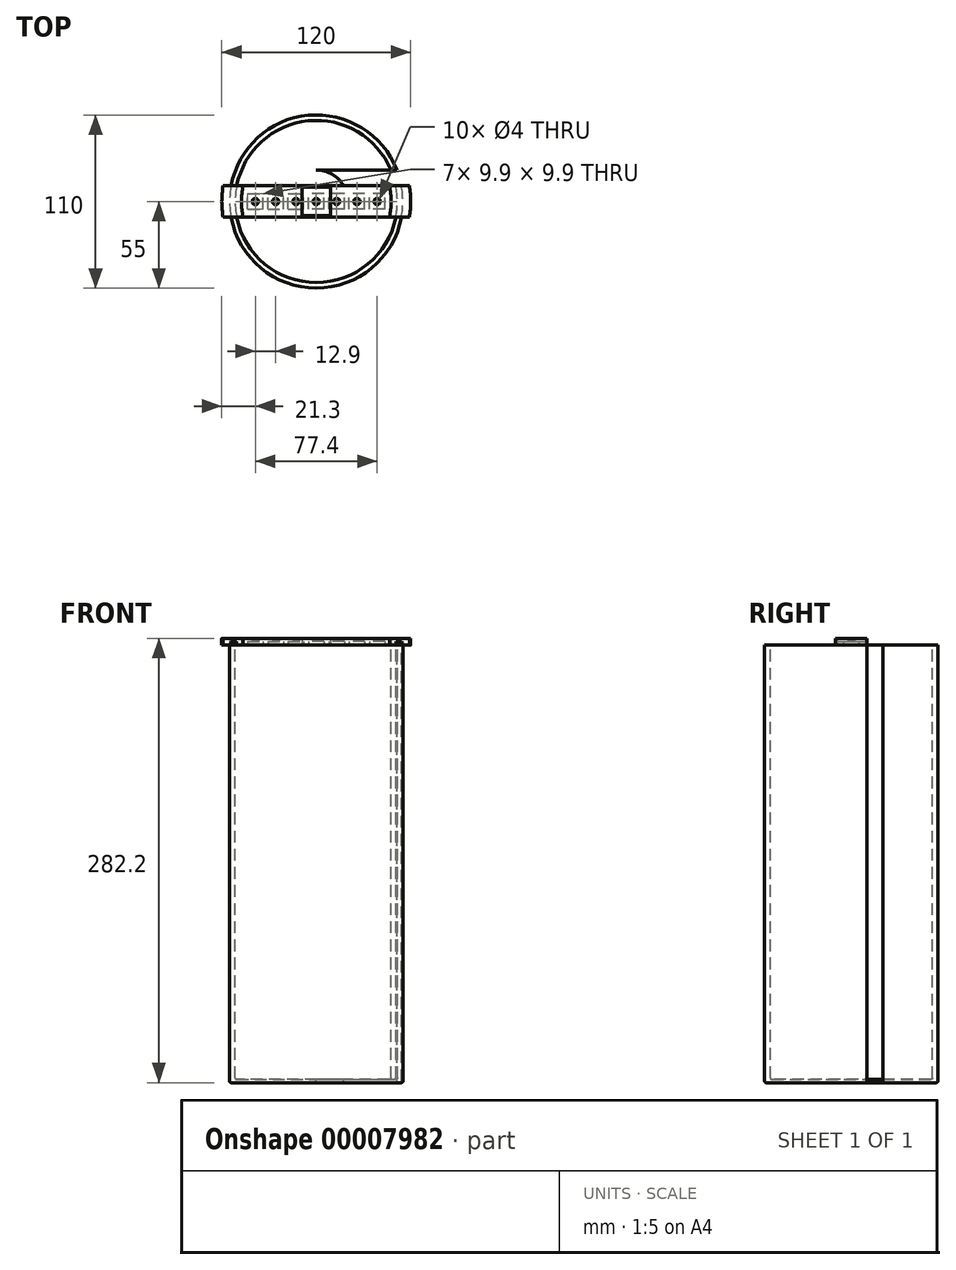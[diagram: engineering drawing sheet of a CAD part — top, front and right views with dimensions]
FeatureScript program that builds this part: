
annotation { "Feature Type Name" : "Feature", "Feature Type Description" : "" }
export const myFeature = defineFeature(function(context is Context, id is Id, definition is map)
    precondition{}
    {
        {
            var Q0;
            Q0=qCreatedBy(makeId("Top.planeOp"),FACE);
            var sketch = newSketch(context, id + "F0", { "sketchPlane" : qUnion([Q0])});
            skCircle(sketch, "E0", {"center": v(0, 0) * mm, "radius": 51.5 * mm});
            skCircle(sketch, "E1", {"center": v(0, 0) * mm, "radius": 4.8 * mm});
            skCircle(sketch, "E2", {"center": v(0, 12.6) * mm, "radius": 4.8 * mm});
            skLineSegment(sketch, "E3", {"start": v(0, 0) * mm, "end": v(0, 33.04) * mm, "construction": true});
            skCircle(sketch, "E4.1.0", {"center": v(-10.91, 6.3) * mm, "radius": 4.8 * mm});
            skCircle(sketch, "E4.2.0", {"center": v(-10.91, -6.3) * mm, "radius": 4.8 * mm});
            skCircle(sketch, "E4.3.0", {"center": v(0, -12.6) * mm, "radius": 4.8 * mm});
            skCircle(sketch, "E4.4.0", {"center": v(10.91, -6.3) * mm, "radius": 4.8 * mm});
            skCircle(sketch, "E4.5.0", {"center": v(10.91, 6.3) * mm, "radius": 4.8 * mm});
            skCircle(sketch, "E5", {"center": v(0, 0) * mm, "radius": 7.8 * mm, "construction": true});
            skCircle(sketch, "E6", {"center": v(0, 0) * mm, "radius": 20 * mm});
            skLineSegment(sketch, "E7.bottom", {"start": v(-65.9, 20) * mm, "end": v(65.9, 20) * mm});
            skLineSegment(sketch, "E7.top", {"start": v(-65.9, -20) * mm, "end": v(65.9, -20) * mm});
            skLineSegment(sketch, "E7.left", {"start": v(-65.9, 20) * mm, "end": v(-65.9, -20) * mm});
            skLineSegment(sketch, "E7.right", {"start": v(65.9, 20) * mm, "end": v(65.9, -20) * mm});
            skLineSegment(sketch, "E8", {"start": v(-65.9, 0) * mm, "end": v(65.9, 0) * mm, "construction": true});
            skCircle(sketch, "E9", {"center": v(0, 0) * mm, "radius": 55 * mm});
            skLineSegment(sketch, "E10", {"start": v(0, 20) * mm, "end": v(0, -20) * mm, "construction": true});
            skCircle(sketch, "E11", {"center": v(0, 0) * mm, "radius": 60 * mm});
            skCircle(sketch, "E12", {"center": v(0, 12.6) * mm, "radius": 1.75 * mm});
            skCircle(sketch, "E13", {"center": v(10.91, 6.3) * mm, "radius": 1.75 * mm});
            skCircle(sketch, "E14", {"center": v(10.91, -6.3) * mm, "radius": 1.75 * mm});
            skCircle(sketch, "E15", {"center": v(0, -12.6) * mm, "radius": 1.75 * mm});
            skCircle(sketch, "E16", {"center": v(-10.91, 6.3) * mm, "radius": 1.75 * mm});
            skCircle(sketch, "E17", {"center": v(-10.91, -6.3) * mm, "radius": 1.75 * mm});
            skCircle(sketch, "E18", {"center": v(0, 0) * mm, "radius": 1.75 * mm});
            skLineSegment(sketch, "E19.bottom", {"start": v(-65.9, -10) * mm, "end": v(-17.32, -10) * mm});
            skLineSegment(sketch, "E19.top", {"start": v(-65.9, 10) * mm, "end": v(-17.32, 10) * mm});
            skLineSegment(sketch, "E19.left", {"start": v(-65.9, -10) * mm, "end": v(-65.9, 10) * mm});
            skLineSegment(sketch, "E19.right", {"start": v(65.9, -10) * mm, "end": v(65.9, 10) * mm});
            skLineSegment(sketch, "E20.trimOffspring", {"start": v(17.32, -10) * mm, "end": v(65.9, -10) * mm});
            skLineSegment(sketch, "E21.trimOffspring", {"start": v(17.32, 10) * mm, "end": v(65.9, 10) * mm});
            skLineSegment(sketch, "E22.bottom", {"start": v(-24, -5) * mm, "end": v(-47.5, -5) * mm});
            skLineSegment(sketch, "E22.top", {"start": v(-24, 5) * mm, "end": v(-47.5, 5) * mm});
            skLineSegment(sketch, "E22.left", {"start": v(-24, -5) * mm, "end": v(-24, 5) * mm});
            skLineSegment(sketch, "E22.right", {"start": v(-47.5, -5) * mm, "end": v(-47.5, 5) * mm});
            skPoint(sketch, "E22.middle", {"position": v(-35.75, 0) * mm});
            skLineSegment(sketch, "E23.MirrorCS", {"start": v(24, 5) * mm, "end": v(47.5, 5) * mm});
            skLineSegment(sketch, "E24.MirrorCS", {"start": v(24, -5) * mm, "end": v(24, 5) * mm});
            skLineSegment(sketch, "E25.MirrorCS", {"start": v(24, -5) * mm, "end": v(47.5, -5) * mm});
            skLineSegment(sketch, "E26.MirrorCS", {"start": v(47.5, -5) * mm, "end": v(47.5, 5) * mm});
            skSolve(sketch);
        }
        {
            var Q0;
            {var subQ0=sQuery(id+"F0.wireOp",EDGE,"E7.bottom");var subQ1=sQuery(id+"F0.wireOp",EDGE,"E0");var subQ2=makeQuery(id+"F0.imprint","INTERSECT",VERTEX,{"disambiguationData":[OD(0.0)],"derivedFrom":[subQ1,subQ0]});Q0=makeQuery(id+"F0.imprint","IMPRINT",FACE,{"disambiguationData":[TD([[makeQuery(id+"F0.imprint","IMPRINT",EDGE,{"disambiguationData":[TD([[subQ2,-1.0]])],"derivedFrom":subQ1}),-1.0]])]});}
            var Q1;
            {var subQ0=sQuery(id+"F0.wireOp",EDGE,"E7.bottom");var subQ1=sQuery(id+"F0.wireOp",EDGE,"E0");var subQ2=makeQuery(id+"F0.imprint","INTERSECT",VERTEX,{"disambiguationData":[OD(1.0)],"derivedFrom":[subQ1,subQ0]});Q1=makeQuery(id+"F0.imprint","IMPRINT",FACE,{"disambiguationData":[TD([[makeQuery(id+"F0.imprint","IMPRINT",EDGE,{"disambiguationData":[TD([[subQ2,-1.0]])],"derivedFrom":subQ1}),-1.0]])]});}
            var Q2;
            {var subQ0=sQuery(id+"F0.wireOp",EDGE,"E19.top");var subQ1=sQuery(id+"F0.wireOp",EDGE,"E0");var subQ2=makeQuery(id+"F0.imprint","INTERSECT",VERTEX,{"derivedFrom":[subQ1,subQ0]});Q2=makeQuery(id+"F0.imprint","IMPRINT",FACE,{"disambiguationData":[TD([[makeQuery(id+"F0.imprint","IMPRINT",EDGE,{"disambiguationData":[TD([[subQ2,-1.0]])],"derivedFrom":subQ1}),-1.0]])]});}
            var Q3;
            {var subQ0=sQuery(id+"F0.wireOp",EDGE,"E19.bottom");var subQ1=sQuery(id+"F0.wireOp",EDGE,"E0");var subQ2=makeQuery(id+"F0.imprint","INTERSECT",VERTEX,{"derivedFrom":[subQ1,subQ0]});Q3=makeQuery(id+"F0.imprint","IMPRINT",FACE,{"disambiguationData":[TD([[makeQuery(id+"F0.imprint","IMPRINT",EDGE,{"disambiguationData":[TD([[subQ2,-1.0]])],"derivedFrom":subQ1}),-1.0]])]});}
            var Q4;
            {var subQ0=sQuery(id+"F0.wireOp",EDGE,"E7.top");var subQ1=sQuery(id+"F0.wireOp",EDGE,"E0");var subQ2=makeQuery(id+"F0.imprint","INTERSECT",VERTEX,{"disambiguationData":[OD(0.0)],"derivedFrom":[subQ1,subQ0]});Q4=makeQuery(id+"F0.imprint","IMPRINT",FACE,{"disambiguationData":[TD([[makeQuery(id+"F0.imprint","IMPRINT",EDGE,{"disambiguationData":[TD([[subQ2,-1.0]])],"derivedFrom":subQ1}),-1.0]])]});}
            var Q5;
            {var subQ0=sQuery(id+"F0.wireOp",EDGE,"E7.top");var subQ1=sQuery(id+"F0.wireOp",EDGE,"E0");var subQ2=makeQuery(id+"F0.imprint","INTERSECT",VERTEX,{"disambiguationData":[OD(1.0)],"derivedFrom":[subQ1,subQ0]});Q5=makeQuery(id+"F0.imprint","IMPRINT",FACE,{"disambiguationData":[TD([[makeQuery(id+"F0.imprint","IMPRINT",EDGE,{"disambiguationData":[TD([[subQ2,-1.0]])],"derivedFrom":subQ1}),-1.0]])]});}
            var Q6;
            {var subQ0=sQuery(id+"F0.wireOp",EDGE,"E21.trimOffspring");var subQ1=sQuery(id+"F0.wireOp",EDGE,"E0");var subQ2=makeQuery(id+"F0.imprint","INTERSECT",VERTEX,{"derivedFrom":[subQ1,subQ0]});Q6=makeQuery(id+"F0.imprint","IMPRINT",FACE,{"disambiguationData":[TD([[makeQuery(id+"F0.imprint","IMPRINT",EDGE,{"disambiguationData":[TD([[subQ2,1.0]])],"derivedFrom":subQ1}),-1.0]])]});}
            var Q7;
            {var subQ0=sQuery(id+"F0.wireOp",EDGE,"E7.bottom");var subQ1=sQuery(id+"F0.wireOp",EDGE,"E0");var subQ2=makeQuery(id+"F0.imprint","INTERSECT",VERTEX,{"disambiguationData":[OD(0.0)],"derivedFrom":[subQ1,subQ0]});Q7=makeQuery(id+"F0.imprint","IMPRINT",FACE,{"disambiguationData":[TD([[makeQuery(id+"F0.imprint","IMPRINT",EDGE,{"disambiguationData":[TD([[subQ2,1.0]])],"derivedFrom":subQ1}),-1.0]])]});}
            var Q8;
            {var subQ0=sQuery(id+"F0.wireOp",EDGE,"E19.top");var subQ1=sQuery(id+"F0.wireOp",EDGE,"E0");var subQ2=makeQuery(id+"F0.imprint","INTERSECT",VERTEX,{"derivedFrom":[subQ1,subQ0]});Q8=makeQuery(id+"F0.imprint","IMPRINT",FACE,{"disambiguationData":[TD([[makeQuery(id+"F0.imprint","IMPRINT",EDGE,{"disambiguationData":[TD([[subQ2,-1.0]])],"derivedFrom":subQ1}),1.0]])]});}
            var Q9;
            Q9=makeQuery(id+"F0.imprint","IMPRINT",FACE,{"disambiguationData":[TD([[makeQuery(id+"F0.imprint","IMPRINT",EDGE,{"derivedFrom":sQuery(id+"F0.wireOp",EDGE,"E4.2.0")}),1.0]])]});
            var Q10;
            {var subQ0=sQuery(id+"F0.wireOp",EDGE,"E7.bottom");var subQ1=sQuery(id+"F0.wireOp",EDGE,"E0");var subQ2=makeQuery(id+"F0.imprint","INTERSECT",VERTEX,{"disambiguationData":[OD(1.0)],"derivedFrom":[subQ1,subQ0]});Q10=makeQuery(id+"F0.imprint","IMPRINT",FACE,{"disambiguationData":[TD([[makeQuery(id+"F0.imprint","IMPRINT",EDGE,{"disambiguationData":[TD([[subQ2,-1.0]])],"derivedFrom":subQ1}),1.0]])]});}
            var Q11;
            {var subQ0=sQuery(id+"F0.wireOp",EDGE,"E7.bottom");var subQ1=sQuery(id+"F0.wireOp",EDGE,"E0");var subQ2=makeQuery(id+"F0.imprint","INTERSECT",VERTEX,{"disambiguationData":[OD(0.0)],"derivedFrom":[subQ1,subQ0]});Q11=makeQuery(id+"F0.imprint","IMPRINT",FACE,{"disambiguationData":[TD([[makeQuery(id+"F0.imprint","IMPRINT",EDGE,{"disambiguationData":[TD([[subQ2,-1.0]])],"derivedFrom":subQ1}),1.0]])]});}
            var Q12;
            {var subQ0=sQuery(id+"F0.wireOp",EDGE,"E19.bottom");var subQ1=sQuery(id+"F0.wireOp",EDGE,"E0");var subQ2=makeQuery(id+"F0.imprint","INTERSECT",VERTEX,{"derivedFrom":[subQ1,subQ0]});Q12=makeQuery(id+"F0.imprint","IMPRINT",FACE,{"disambiguationData":[TD([[makeQuery(id+"F0.imprint","IMPRINT",EDGE,{"disambiguationData":[TD([[subQ2,-1.0]])],"derivedFrom":subQ1}),1.0]])]});}
            var Q13;
            Q13=makeQuery(id+"F0.imprint","IMPRINT",FACE,{"disambiguationData":[TD([[makeQuery(id+"F0.imprint","IMPRINT",EDGE,{"derivedFrom":sQuery(id+"F0.wireOp",EDGE,"E17")}),1.0]])]});
            var Q14;
            {var subQ0=sQuery(id+"F0.wireOp",EDGE,"E7.top");var subQ1=sQuery(id+"F0.wireOp",EDGE,"E0");var subQ2=makeQuery(id+"F0.imprint","INTERSECT",VERTEX,{"disambiguationData":[OD(0.0)],"derivedFrom":[subQ1,subQ0]});Q14=makeQuery(id+"F0.imprint","IMPRINT",FACE,{"disambiguationData":[TD([[makeQuery(id+"F0.imprint","IMPRINT",EDGE,{"disambiguationData":[TD([[subQ2,-1.0]])],"derivedFrom":subQ1}),1.0]])]});}
            var Q15;
            {var subQ0=sQuery(id+"F0.wireOp",EDGE,"E7.bottom");var subQ1=sQuery(id+"F0.wireOp",EDGE,"E0");var subQ2=makeQuery(id+"F0.imprint","INTERSECT",VERTEX,{"disambiguationData":[OD(0.0)],"derivedFrom":[subQ1,subQ0]});Q15=makeQuery(id+"F0.imprint","IMPRINT",FACE,{"disambiguationData":[TD([[makeQuery(id+"F0.imprint","IMPRINT",EDGE,{"disambiguationData":[TD([[subQ2,1.0]])],"derivedFrom":subQ1}),1.0]])]});}
            var Q16;
            {var subQ0=sQuery(id+"F0.wireOp",EDGE,"E21.trimOffspring");var subQ1=sQuery(id+"F0.wireOp",EDGE,"E0");var subQ2=makeQuery(id+"F0.imprint","INTERSECT",VERTEX,{"derivedFrom":[subQ1,subQ0]});Q16=makeQuery(id+"F0.imprint","IMPRINT",FACE,{"disambiguationData":[TD([[makeQuery(id+"F0.imprint","IMPRINT",EDGE,{"disambiguationData":[TD([[subQ2,1.0]])],"derivedFrom":subQ1}),1.0]])]});}
            var Q17;
            {var subQ0=sQuery(id+"F0.wireOp",EDGE,"E7.top");var subQ1=sQuery(id+"F0.wireOp",EDGE,"E0");var subQ2=makeQuery(id+"F0.imprint","INTERSECT",VERTEX,{"disambiguationData":[OD(1.0)],"derivedFrom":[subQ1,subQ0]});Q17=makeQuery(id+"F0.imprint","IMPRINT",FACE,{"disambiguationData":[TD([[makeQuery(id+"F0.imprint","IMPRINT",EDGE,{"disambiguationData":[TD([[subQ2,-1.0]])],"derivedFrom":subQ1}),1.0]])]});}
            var Q18;
            Q18=makeQuery(id+"F0.imprint","IMPRINT",FACE,{"disambiguationData":[TD([[makeQuery(id+"F0.imprint","IMPRINT",EDGE,{"derivedFrom":sQuery(id+"F0.wireOp",EDGE,"E1")}),-1.0]])]});
            var Q19;
            Q19=makeQuery(id+"F0.imprint","IMPRINT",FACE,{"disambiguationData":[TD([[makeQuery(id+"F0.imprint","IMPRINT",EDGE,{"derivedFrom":sQuery(id+"F0.wireOp",EDGE,"E4.1.0")}),1.0]])]});
            var Q20;
            Q20=makeQuery(id+"F0.imprint","IMPRINT",FACE,{"disambiguationData":[TD([[makeQuery(id+"F0.imprint","IMPRINT",EDGE,{"derivedFrom":sQuery(id+"F0.wireOp",EDGE,"E2")}),1.0]])]});
            var Q21;
            Q21=makeQuery(id+"F0.imprint","IMPRINT",FACE,{"disambiguationData":[TD([[makeQuery(id+"F0.imprint","IMPRINT",EDGE,{"derivedFrom":sQuery(id+"F0.wireOp",EDGE,"E1")}),1.0]])]});
            var Q22;
            Q22=makeQuery(id+"F0.imprint","IMPRINT",FACE,{"disambiguationData":[TD([[makeQuery(id+"F0.imprint","IMPRINT",EDGE,{"derivedFrom":sQuery(id+"F0.wireOp",EDGE,"E4.5.0")}),1.0]])]});
            var Q23;
            Q23=makeQuery(id+"F0.imprint","IMPRINT",FACE,{"disambiguationData":[TD([[makeQuery(id+"F0.imprint","IMPRINT",EDGE,{"derivedFrom":sQuery(id+"F0.wireOp",EDGE,"E4.4.0")}),1.0]])]});
            var Q24;
            Q24=makeQuery(id+"F0.imprint","IMPRINT",FACE,{"disambiguationData":[TD([[makeQuery(id+"F0.imprint","IMPRINT",EDGE,{"derivedFrom":sQuery(id+"F0.wireOp",EDGE,"E4.3.0")}),1.0]])]});
            var Q25;
            Q25=makeQuery(id+"F0.imprint","IMPRINT",FACE,{"disambiguationData":[TD([[makeQuery(id+"F0.imprint","IMPRINT",EDGE,{"derivedFrom":sQuery(id+"F0.wireOp",EDGE,"E16")}),1.0]])]});
            var Q26;
            Q26=makeQuery(id+"F0.imprint","IMPRINT",FACE,{"disambiguationData":[TD([[makeQuery(id+"F0.imprint","IMPRINT",EDGE,{"derivedFrom":sQuery(id+"F0.wireOp",EDGE,"E12")}),1.0]])]});
            var Q27;
            Q27=makeQuery(id+"F0.imprint","IMPRINT",FACE,{"disambiguationData":[TD([[makeQuery(id+"F0.imprint","IMPRINT",EDGE,{"derivedFrom":sQuery(id+"F0.wireOp",EDGE,"E13")}),1.0]])]});
            var Q28;
            Q28=makeQuery(id+"F0.imprint","IMPRINT",FACE,{"disambiguationData":[TD([[makeQuery(id+"F0.imprint","IMPRINT",EDGE,{"derivedFrom":sQuery(id+"F0.wireOp",EDGE,"E14")}),1.0]])]});
            var Q29;
            Q29=makeQuery(id+"F0.imprint","IMPRINT",FACE,{"disambiguationData":[TD([[makeQuery(id+"F0.imprint","IMPRINT",EDGE,{"derivedFrom":sQuery(id+"F0.wireOp",EDGE,"E18")}),1.0]])]});
            var Q30;
            Q30=makeQuery(id+"F0.imprint","IMPRINT",FACE,{"disambiguationData":[TD([[makeQuery(id+"F0.imprint","IMPRINT",EDGE,{"derivedFrom":sQuery(id+"F0.wireOp",EDGE,"E15")}),1.0]])]});
            var Q31;
            Q31=makeQuery(id+"F0.imprint","IMPRINT",FACE,{"disambiguationData":[TD([[makeQuery(id+"F0.imprint","IMPRINT",EDGE,{"derivedFrom":sQuery(id+"F0.wireOp",EDGE,"E22.bottom")}),-1.0]])]});
            var Q32;
            Q32=makeQuery(id+"F0.imprint","IMPRINT",FACE,{"disambiguationData":[TD([[makeQuery(id+"F0.imprint","IMPRINT",EDGE,{"derivedFrom":sQuery(id+"F0.wireOp",EDGE,"E23.MirrorCS")}),-1.0]])]});
            extrude(context, id + "F1", {"entities" : qUnion([Q0, Q1, Q2, Q3, Q4, Q5, Q6, Q7, Q8, Q9, Q10, Q11, Q12, Q13, Q14, Q15, Q16, Q17, Q18, Q19, Q20, Q21, Q22, Q23, Q24, Q25, Q26, Q27, Q28, Q29, Q30, Q31, Q32]), "oppositeDirection" : true, "depth" : 278 * mm});
        }
        {
            var Q0;
            {var subQ0=sQuery(id+"F0.wireOp",EDGE,"E7.bottom");var subQ1=sQuery(id+"F0.wireOp",EDGE,"E0");var subQ2=makeQuery(id+"F0.imprint","INTERSECT",VERTEX,{"disambiguationData":[OD(0.0)],"derivedFrom":[subQ1,subQ0]});Q0=makeQuery(id+"F0.imprint","IMPRINT",FACE,{"disambiguationData":[TD([[makeQuery(id+"F0.imprint","IMPRINT",EDGE,{"disambiguationData":[TD([[subQ2,-1.0]])],"derivedFrom":subQ1}),1.0]])]});}
            var Q1;
            {var subQ0=sQuery(id+"F0.wireOp",EDGE,"E7.bottom");var subQ1=sQuery(id+"F0.wireOp",EDGE,"E0");var subQ2=makeQuery(id+"F0.imprint","INTERSECT",VERTEX,{"disambiguationData":[OD(0.0)],"derivedFrom":[subQ1,subQ0]});Q1=makeQuery(id+"F0.imprint","IMPRINT",FACE,{"disambiguationData":[TD([[makeQuery(id+"F0.imprint","IMPRINT",EDGE,{"disambiguationData":[TD([[subQ2,1.0]])],"derivedFrom":subQ1}),1.0]])]});}
            var Q2;
            {var subQ0=sQuery(id+"F0.wireOp",EDGE,"E21.trimOffspring");var subQ1=sQuery(id+"F0.wireOp",EDGE,"E0");var subQ2=makeQuery(id+"F0.imprint","INTERSECT",VERTEX,{"derivedFrom":[subQ1,subQ0]});Q2=makeQuery(id+"F0.imprint","IMPRINT",FACE,{"disambiguationData":[TD([[makeQuery(id+"F0.imprint","IMPRINT",EDGE,{"disambiguationData":[TD([[subQ2,1.0]])],"derivedFrom":subQ1}),1.0]])]});}
            var Q3;
            {var subQ0=sQuery(id+"F0.wireOp",EDGE,"E7.top");var subQ1=sQuery(id+"F0.wireOp",EDGE,"E0");var subQ2=makeQuery(id+"F0.imprint","INTERSECT",VERTEX,{"disambiguationData":[OD(1.0)],"derivedFrom":[subQ1,subQ0]});Q3=makeQuery(id+"F0.imprint","IMPRINT",FACE,{"disambiguationData":[TD([[makeQuery(id+"F0.imprint","IMPRINT",EDGE,{"disambiguationData":[TD([[subQ2,-1.0]])],"derivedFrom":subQ1}),1.0]])]});}
            var Q4;
            {var subQ0=sQuery(id+"F0.wireOp",EDGE,"E7.top");var subQ1=sQuery(id+"F0.wireOp",EDGE,"E0");var subQ2=makeQuery(id+"F0.imprint","INTERSECT",VERTEX,{"disambiguationData":[OD(0.0)],"derivedFrom":[subQ1,subQ0]});Q4=makeQuery(id+"F0.imprint","IMPRINT",FACE,{"disambiguationData":[TD([[makeQuery(id+"F0.imprint","IMPRINT",EDGE,{"disambiguationData":[TD([[subQ2,-1.0]])],"derivedFrom":subQ1}),1.0]])]});}
            var Q5;
            {var subQ0=sQuery(id+"F0.wireOp",EDGE,"E19.bottom");var subQ1=sQuery(id+"F0.wireOp",EDGE,"E0");var subQ2=makeQuery(id+"F0.imprint","INTERSECT",VERTEX,{"derivedFrom":[subQ1,subQ0]});Q5=makeQuery(id+"F0.imprint","IMPRINT",FACE,{"disambiguationData":[TD([[makeQuery(id+"F0.imprint","IMPRINT",EDGE,{"disambiguationData":[TD([[subQ2,-1.0]])],"derivedFrom":subQ1}),1.0]])]});}
            var Q6;
            {var subQ0=sQuery(id+"F0.wireOp",EDGE,"E7.bottom");var subQ1=sQuery(id+"F0.wireOp",EDGE,"E0");var subQ2=makeQuery(id+"F0.imprint","INTERSECT",VERTEX,{"disambiguationData":[OD(1.0)],"derivedFrom":[subQ1,subQ0]});Q6=makeQuery(id+"F0.imprint","IMPRINT",FACE,{"disambiguationData":[TD([[makeQuery(id+"F0.imprint","IMPRINT",EDGE,{"disambiguationData":[TD([[subQ2,-1.0]])],"derivedFrom":subQ1}),1.0]])]});}
            var Q7;
            {var subQ0=sQuery(id+"F0.wireOp",EDGE,"E19.top");var subQ1=sQuery(id+"F0.wireOp",EDGE,"E0");var subQ2=makeQuery(id+"F0.imprint","INTERSECT",VERTEX,{"derivedFrom":[subQ1,subQ0]});Q7=makeQuery(id+"F0.imprint","IMPRINT",FACE,{"disambiguationData":[TD([[makeQuery(id+"F0.imprint","IMPRINT",EDGE,{"disambiguationData":[TD([[subQ2,-1.0]])],"derivedFrom":subQ1}),1.0]])]});}
            var Q8;
            Q8=makeQuery(id+"F0.imprint","IMPRINT",FACE,{"disambiguationData":[TD([[makeQuery(id+"F0.imprint","IMPRINT",EDGE,{"derivedFrom":sQuery(id+"F0.wireOp",EDGE,"E1")}),-1.0]])]});
            var Q9;
            Q9=makeQuery(id+"F0.imprint","IMPRINT",FACE,{"disambiguationData":[TD([[makeQuery(id+"F0.imprint","IMPRINT",EDGE,{"derivedFrom":sQuery(id+"F0.wireOp",EDGE,"E4.4.0")}),1.0]])]});
            var Q10;
            Q10=makeQuery(id+"F0.imprint","IMPRINT",FACE,{"disambiguationData":[TD([[makeQuery(id+"F0.imprint","IMPRINT",EDGE,{"derivedFrom":sQuery(id+"F0.wireOp",EDGE,"E14")}),1.0]])]});
            var Q11;
            Q11=makeQuery(id+"F0.imprint","IMPRINT",FACE,{"disambiguationData":[TD([[makeQuery(id+"F0.imprint","IMPRINT",EDGE,{"derivedFrom":sQuery(id+"F0.wireOp",EDGE,"E13")}),1.0]])]});
            var Q12;
            Q12=makeQuery(id+"F0.imprint","IMPRINT",FACE,{"disambiguationData":[TD([[makeQuery(id+"F0.imprint","IMPRINT",EDGE,{"derivedFrom":sQuery(id+"F0.wireOp",EDGE,"E4.5.0")}),1.0]])]});
            var Q13;
            Q13=makeQuery(id+"F0.imprint","IMPRINT",FACE,{"disambiguationData":[TD([[makeQuery(id+"F0.imprint","IMPRINT",EDGE,{"derivedFrom":sQuery(id+"F0.wireOp",EDGE,"E2")}),1.0]])]});
            var Q14;
            Q14=makeQuery(id+"F0.imprint","IMPRINT",FACE,{"disambiguationData":[TD([[makeQuery(id+"F0.imprint","IMPRINT",EDGE,{"derivedFrom":sQuery(id+"F0.wireOp",EDGE,"E12")}),1.0]])]});
            var Q15;
            Q15=makeQuery(id+"F0.imprint","IMPRINT",FACE,{"disambiguationData":[TD([[makeQuery(id+"F0.imprint","IMPRINT",EDGE,{"derivedFrom":sQuery(id+"F0.wireOp",EDGE,"E4.1.0")}),1.0]])]});
            var Q16;
            Q16=makeQuery(id+"F0.imprint","IMPRINT",FACE,{"disambiguationData":[TD([[makeQuery(id+"F0.imprint","IMPRINT",EDGE,{"derivedFrom":sQuery(id+"F0.wireOp",EDGE,"E16")}),1.0]])]});
            var Q17;
            Q17=makeQuery(id+"F0.imprint","IMPRINT",FACE,{"disambiguationData":[TD([[makeQuery(id+"F0.imprint","IMPRINT",EDGE,{"derivedFrom":sQuery(id+"F0.wireOp",EDGE,"E4.2.0")}),1.0]])]});
            var Q18;
            Q18=makeQuery(id+"F0.imprint","IMPRINT",FACE,{"disambiguationData":[TD([[makeQuery(id+"F0.imprint","IMPRINT",EDGE,{"derivedFrom":sQuery(id+"F0.wireOp",EDGE,"E17")}),1.0]])]});
            var Q19;
            Q19=makeQuery(id+"F0.imprint","IMPRINT",FACE,{"disambiguationData":[TD([[makeQuery(id+"F0.imprint","IMPRINT",EDGE,{"derivedFrom":sQuery(id+"F0.wireOp",EDGE,"E4.3.0")}),1.0]])]});
            var Q20;
            Q20=makeQuery(id+"F0.imprint","IMPRINT",FACE,{"disambiguationData":[TD([[makeQuery(id+"F0.imprint","IMPRINT",EDGE,{"derivedFrom":sQuery(id+"F0.wireOp",EDGE,"E15")}),1.0]])]});
            var Q21;
            Q21=makeQuery(id+"F0.imprint","IMPRINT",FACE,{"disambiguationData":[TD([[makeQuery(id+"F0.imprint","IMPRINT",EDGE,{"derivedFrom":sQuery(id+"F0.wireOp",EDGE,"E1")}),1.0]])]});
            var Q22;
            Q22=makeQuery(id+"F0.imprint","IMPRINT",FACE,{"disambiguationData":[TD([[makeQuery(id+"F0.imprint","IMPRINT",EDGE,{"derivedFrom":sQuery(id+"F0.wireOp",EDGE,"E18")}),1.0]])]});
            var Q23;
            Q23=makeQuery(id+"F0.imprint","IMPRINT",FACE,{"disambiguationData":[TD([[makeQuery(id+"F0.imprint","IMPRINT",EDGE,{"derivedFrom":sQuery(id+"F0.wireOp",EDGE,"E22.bottom")}),-1.0]])]});
            var Q24;
            Q24=makeQuery(id+"F0.imprint","IMPRINT",FACE,{"disambiguationData":[TD([[makeQuery(id+"F0.imprint","IMPRINT",EDGE,{"derivedFrom":sQuery(id+"F0.wireOp",EDGE,"E23.MirrorCS")}),-1.0]])]});
            extrude(context, id + "F2", {"entities" : qUnion([Q0, Q1, Q2, Q3, Q4, Q5, Q6, Q7, Q8, Q9, Q10, Q11, Q12, Q13, Q14, Q15, Q16, Q17, Q18, Q19, Q20, Q21, Q22, Q23, Q24]), "operationType" : NewBodyOperationType.REMOVE, "oppositeDirection" : true, "depth" : 276 * mm});
        }
        {
            var Q0;
            Q0=makeQuery(id+"F2.boolean.opBoolean","COPY",EDGE,{"derivedFrom":makeQuery(id+"F2.opExtrude","CAP_EDGE",EDGE,{"disambiguationData":[OSD([sQuery(id+"F0.wireOp",EDGE,"E0")])],"isStart":false})});
            var Q1;
            Q1=makeQuery(id+"F1.opExtrude","CAP_EDGE",EDGE,{"disambiguationData":[OSD([sQuery(id+"F0.wireOp",EDGE,"E9")])],"isStart":false});
            fillet(context, id + "F3", {"entities" : qUnion([Q0, Q1]), "radius" : 1 * mm, "tangentPropagation" : true, "allowEdgeOverflow" : false});
        }
        {
            var Q0;
            Q0=qCreatedBy(makeId("Top.planeOp"),FACE);
            var sketch = newSketch(context, id + "F4", { "sketchPlane" : qUnion([Q0])});
            skLineSegment(sketch, "E27.0", {"start": v(-59.16, 10) * mm, "end": v(-17.32, 10) * mm});
            skLineSegment(sketch, "E27.1", {"start": v(17.32, 10) * mm, "end": v(59.16, 10) * mm});
            skLineSegment(sketch, "E27.2", {"start": v(17.32, -10) * mm, "end": v(59.16, -10) * mm});
            skLineSegment(sketch, "E27.3", {"start": v(-59.16, -10) * mm, "end": v(-17.32, -10) * mm});
            skCircle(sketch, "E27.4", {"center": v(0, 0) * mm, "radius": 60 * mm});
            skCircle(sketch, "E27.5", {"center": v(0, 0) * mm, "radius": 51.5 * mm});
            skCircle(sketch, "E27.6", {"center": v(0, 0) * mm, "radius": 55 * mm});
            skLineSegment(sketch, "E28.0", {"start": v(0, 0) * mm, "end": v(0, 33.04) * mm, "construction": true});
            skLineSegment(sketch, "E28.1", {"start": v(0, 20) * mm, "end": v(0, -20) * mm, "construction": true});
            skLineSegment(sketch, "E29", {"start": v(-17.32, 10) * mm, "end": v(17.32, 10) * mm});
            skLineSegment(sketch, "E30", {"start": v(-17.32, -10) * mm, "end": v(17.32, -10) * mm});
            skCircle(sketch, "E31", {"center": v(0, 0) * mm, "radius": 47.5 * mm});
            skLineSegment(sketch, "E32.bottom", {"start": v(4.95, -4.95) * mm, "end": v(-4.95, -4.95) * mm});
            skLineSegment(sketch, "E32.top", {"start": v(4.95, 4.95) * mm, "end": v(-4.95, 4.95) * mm});
            skLineSegment(sketch, "E32.left", {"start": v(4.95, -4.95) * mm, "end": v(4.95, 4.95) * mm});
            skLineSegment(sketch, "E32.right", {"start": v(-4.95, -4.95) * mm, "end": v(-4.95, 4.95) * mm});
            skLineSegment(sketch, "E33.1.0.0", {"start": v(17.85, 4.95) * mm, "end": v(7.95, 4.95) * mm});
            skLineSegment(sketch, "E33.1.0.1", {"start": v(17.85, -4.95) * mm, "end": v(17.85, 4.95) * mm});
            skLineSegment(sketch, "E33.1.0.2", {"start": v(17.85, -4.95) * mm, "end": v(7.95, -4.95) * mm});
            skLineSegment(sketch, "E33.1.0.3", {"start": v(7.95, -4.95) * mm, "end": v(7.95, 4.95) * mm});
            skLineSegment(sketch, "E33.2.0.0", {"start": v(30.75, 4.95) * mm, "end": v(20.85, 4.95) * mm});
            skLineSegment(sketch, "E33.2.0.1", {"start": v(30.75, -4.95) * mm, "end": v(30.75, 4.95) * mm});
            skLineSegment(sketch, "E33.2.0.2", {"start": v(30.75, -4.95) * mm, "end": v(20.85, -4.95) * mm});
            skLineSegment(sketch, "E33.2.0.3", {"start": v(20.85, -4.95) * mm, "end": v(20.85, 4.95) * mm});
            skLineSegment(sketch, "E33.3.0.0", {"start": v(43.65, 4.95) * mm, "end": v(33.75, 4.95) * mm});
            skLineSegment(sketch, "E33.3.0.1", {"start": v(43.65, -4.95) * mm, "end": v(43.65, 4.95) * mm});
            skLineSegment(sketch, "E33.3.0.2", {"start": v(43.65, -4.95) * mm, "end": v(33.75, -4.95) * mm});
            skLineSegment(sketch, "E33.3.0.3", {"start": v(33.75, -4.95) * mm, "end": v(33.75, 4.95) * mm});
            skLineSegment(sketch, "E33.direction1", {"start": v(-4.95, 4.95) * mm, "end": v(7.95, 4.95) * mm, "construction": true});
            skLineSegment(sketch, "E34.MirrorCS", {"start": v(-17.85, 4.95) * mm, "end": v(-7.95, 4.95) * mm});
            skLineSegment(sketch, "E35.MirrorCS", {"start": v(-17.85, -4.95) * mm, "end": v(-17.85, 4.95) * mm});
            skLineSegment(sketch, "E36.MirrorCS", {"start": v(-17.85, -4.95) * mm, "end": v(-7.95, -4.95) * mm});
            skLineSegment(sketch, "E37.MirrorCS", {"start": v(-7.95, -4.95) * mm, "end": v(-7.95, 4.95) * mm});
            skLineSegment(sketch, "E38.MirrorCS", {"start": v(-20.85, -4.95) * mm, "end": v(-20.85, 4.95) * mm});
            skLineSegment(sketch, "E39.MirrorCS", {"start": v(-30.75, 4.95) * mm, "end": v(-20.85, 4.95) * mm});
            skLineSegment(sketch, "E40.MirrorCS", {"start": v(-30.75, -4.95) * mm, "end": v(-20.85, -4.95) * mm});
            skLineSegment(sketch, "E41.MirrorCS", {"start": v(-30.75, -4.95) * mm, "end": v(-30.75, 4.95) * mm});
            skLineSegment(sketch, "E42.MirrorCS", {"start": v(-33.75, -4.95) * mm, "end": v(-33.75, 4.95) * mm});
            skLineSegment(sketch, "E43.MirrorCS", {"start": v(-43.65, -4.95) * mm, "end": v(-33.75, -4.95) * mm});
            skLineSegment(sketch, "E44.MirrorCS", {"start": v(-43.65, 4.95) * mm, "end": v(-33.75, 4.95) * mm});
            skLineSegment(sketch, "E45.MirrorCS", {"start": v(-43.65, -4.95) * mm, "end": v(-43.65, 4.95) * mm});
            skCircle(sketch, "E46", {"center": v(0, 0) * mm, "radius": 2 * mm});
            skCircle(sketch, "E47.1.0.0", {"center": v(12.9, 0) * mm, "radius": 2 * mm});
            skCircle(sketch, "E47.2.0.0", {"center": v(25.8, 0) * mm, "radius": 2 * mm});
            skCircle(sketch, "E47.3.0.0", {"center": v(38.7, 0) * mm, "radius": 2 * mm});
            skLineSegment(sketch, "E47.direction1", {"start": v(0, 0) * mm, "end": v(12.9, 0) * mm, "construction": true});
            skCircle(sketch, "E48.MirrorC", {"center": v(-12.9, 0) * mm, "radius": 2 * mm});
            skCircle(sketch, "E49.MirrorC", {"center": v(-25.8, 0) * mm, "radius": 2 * mm});
            skCircle(sketch, "E50.MirrorC", {"center": v(-38.7, 0) * mm, "radius": 2 * mm});
            skSolve(sketch);
        }
        {
            var Q0;
            {var subQ0=sQuery(id+"F4.wireOp",EDGE,"E29");Q0=makeQuery(id+"F4.imprint","IMPRINT",FACE,{"disambiguationData":[TD([[makeQuery(id+"F4.imprint","IMPRINT",EDGE,{"derivedFrom":subQ0}),-1.0]])]});}
            var Q1;
            {var subQ0=sQuery(id+"F4.wireOp",EDGE,"E27.5");var subQ1=sQuery(id+"F4.wireOp",EDGE,"E27.0");var subQ2=makeQuery(id+"F4.imprint","INTERSECT",VERTEX,{"derivedFrom":[subQ1,subQ0]});Q1=makeQuery(id+"F4.imprint","IMPRINT",FACE,{"disambiguationData":[TD([[makeQuery(id+"F4.imprint","IMPRINT",EDGE,{"disambiguationData":[TD([[subQ2,-1.0]])],"derivedFrom":subQ1}),-1.0]])]});}
            var Q2;
            {var subQ0=sQuery(id+"F4.wireOp",EDGE,"E27.4");var subQ1=sQuery(id+"F4.wireOp",EDGE,"E27.0");var subQ2=makeQuery(id+"F4.imprint","INTERSECT",VERTEX,{"derivedFrom":[subQ1,subQ0]});Q2=makeQuery(id+"F4.imprint","IMPRINT",FACE,{"disambiguationData":[TD([[makeQuery(id+"F4.imprint","IMPRINT",EDGE,{"disambiguationData":[TD([[subQ2,-1.0]])],"derivedFrom":subQ1}),-1.0]])]});}
            var Q3;
            {var subQ0=sQuery(id+"F4.wireOp",EDGE,"E27.6");var subQ1=sQuery(id+"F4.wireOp",EDGE,"E27.0");var subQ2=makeQuery(id+"F4.imprint","INTERSECT",VERTEX,{"derivedFrom":[subQ1,subQ0]});Q3=makeQuery(id+"F4.imprint","IMPRINT",FACE,{"disambiguationData":[TD([[makeQuery(id+"F4.imprint","IMPRINT",EDGE,{"disambiguationData":[TD([[subQ2,-1.0]])],"derivedFrom":subQ1}),-1.0]])]});}
            var Q4;
            {var subQ0=sQuery(id+"F4.wireOp",EDGE,"E31");var subQ1=sQuery(id+"F4.wireOp",EDGE,"E27.1");var subQ2=makeQuery(id+"F4.imprint","INTERSECT",VERTEX,{"derivedFrom":[subQ1,subQ0]});Q4=makeQuery(id+"F4.imprint","IMPRINT",FACE,{"disambiguationData":[TD([[makeQuery(id+"F4.imprint","IMPRINT",EDGE,{"disambiguationData":[TD([[subQ2,-1.0]])],"derivedFrom":subQ1}),-1.0]])]});}
            var Q5;
            {var subQ0=sQuery(id+"F4.wireOp",EDGE,"E27.5");var subQ1=sQuery(id+"F4.wireOp",EDGE,"E27.1");var subQ2=makeQuery(id+"F4.imprint","INTERSECT",VERTEX,{"derivedFrom":[subQ1,subQ0]});Q5=makeQuery(id+"F4.imprint","IMPRINT",FACE,{"disambiguationData":[TD([[makeQuery(id+"F4.imprint","IMPRINT",EDGE,{"disambiguationData":[TD([[subQ2,-1.0]])],"derivedFrom":subQ1}),-1.0]])]});}
            var Q6;
            {var subQ0=sQuery(id+"F4.wireOp",EDGE,"E27.4");var subQ1=sQuery(id+"F4.wireOp",EDGE,"E27.1");var subQ2=makeQuery(id+"F4.imprint","INTERSECT",VERTEX,{"derivedFrom":[subQ1,subQ0]});Q6=makeQuery(id+"F4.imprint","IMPRINT",FACE,{"disambiguationData":[TD([[makeQuery(id+"F4.imprint","IMPRINT",EDGE,{"disambiguationData":[TD([[subQ2,1.0]])],"derivedFrom":subQ1}),-1.0]])]});}
            var Q7;
            Q7=makeQuery(id+"F4.imprint","IMPRINT",FACE,{"disambiguationData":[TD([[makeQuery(id+"F4.imprint","IMPRINT",EDGE,{"derivedFrom":sQuery(id+"F4.wireOp",EDGE,"E42.MirrorCS")}),1.0]])]});
            var Q8;
            Q8=makeQuery(id+"F4.imprint","IMPRINT",FACE,{"disambiguationData":[TD([[makeQuery(id+"F4.imprint","IMPRINT",EDGE,{"derivedFrom":sQuery(id+"F4.wireOp",EDGE,"E38.MirrorCS")}),1.0]])]});
            var Q9;
            Q9=makeQuery(id+"F4.imprint","IMPRINT",FACE,{"disambiguationData":[TD([[makeQuery(id+"F4.imprint","IMPRINT",EDGE,{"derivedFrom":sQuery(id+"F4.wireOp",EDGE,"E34.MirrorCS")}),-1.0]])]});
            var Q10;
            Q10=makeQuery(id+"F4.imprint","IMPRINT",FACE,{"disambiguationData":[TD([[makeQuery(id+"F4.imprint","IMPRINT",EDGE,{"derivedFrom":sQuery(id+"F4.wireOp",EDGE,"E32.bottom")}),-1.0]])]});
            var Q11;
            Q11=makeQuery(id+"F4.imprint","IMPRINT",FACE,{"disambiguationData":[TD([[makeQuery(id+"F4.imprint","IMPRINT",EDGE,{"derivedFrom":sQuery(id+"F4.wireOp",EDGE,"E33.1.0.0")}),1.0]])]});
            var Q12;
            Q12=makeQuery(id+"F4.imprint","IMPRINT",FACE,{"disambiguationData":[TD([[makeQuery(id+"F4.imprint","IMPRINT",EDGE,{"derivedFrom":sQuery(id+"F4.wireOp",EDGE,"E33.2.0.0")}),1.0]])]});
            var Q13;
            Q13=makeQuery(id+"F4.imprint","IMPRINT",FACE,{"disambiguationData":[TD([[makeQuery(id+"F4.imprint","IMPRINT",EDGE,{"derivedFrom":sQuery(id+"F4.wireOp",EDGE,"E33.3.0.0")}),1.0]])]});
            extrude(context, id + "F5", {"entities" : qUnion([Q0, Q1, Q2, Q3, Q4, Q5, Q6, Q7, Q8, Q9, Q10, Q11, Q12, Q13]), "depth" : 4.2 * mm});
        }
        {
            var Q0;
            Q0=makeQuery(id+"F4.imprint","IMPRINT",FACE,{"disambiguationData":[TD([[makeQuery(id+"F4.imprint","IMPRINT",EDGE,{"derivedFrom":sQuery(id+"F4.wireOp",EDGE,"8075f1d4-70f9-4dd5-8ec3-b5ab89f9c9bf0.MirrorC")}),1.0]])]});
            var Q1;
            Q1=makeQuery(id+"F4.imprint","IMPRINT",FACE,{"disambiguationData":[TD([[makeQuery(id+"F4.imprint","IMPRINT",EDGE,{"derivedFrom":sQuery(id+"F4.wireOp",EDGE,"205f96f4-c8fc-4229-a65b-f430040cf765.2.0.0")}),-1.0]])]});
            var Q2;
            Q2=makeQuery(id+"F4.imprint","IMPRINT",FACE,{"disambiguationData":[TD([[makeQuery(id+"F4.imprint","IMPRINT",EDGE,{"derivedFrom":sQuery(id+"F4.wireOp",EDGE,"8d914cb3-9dea-42ac-bea7-a907530d0bcd.1")}),-1.0]])]});
            var Q3;
            Q3=makeQuery(id+"F4.imprint","IMPRINT",FACE,{"disambiguationData":[TD([[makeQuery(id+"F4.imprint","IMPRINT",EDGE,{"derivedFrom":sQuery(id+"F4.wireOp",EDGE,"04902287-73d8-48a6-80b9-1e851868ecae0.MirrorC")}),-1.0]])]});
            var Q4;
            Q4=makeQuery(id+"F4.imprint","IMPRINT",FACE,{"disambiguationData":[TD([[makeQuery(id+"F4.imprint","IMPRINT",EDGE,{"derivedFrom":sQuery(id+"F4.wireOp",EDGE,"8075f1d4-70f9-4dd5-8ec3-b5ab89f9c9bf0.MirrorC")}),-1.0]])]});
            var Q5;
            Q5=makeQuery(id+"F4.imprint","IMPRINT",FACE,{"disambiguationData":[TD([[makeQuery(id+"F4.imprint","IMPRINT",EDGE,{"derivedFrom":sQuery(id+"F4.wireOp",EDGE,"de049f4f-b769-4421-8bf6-e8ee1ef1f7560.MirrorC")}),-1.0]])]});
            var Q6;
            Q6=makeQuery(id+"F4.imprint","IMPRINT",FACE,{"disambiguationData":[TD([[makeQuery(id+"F4.imprint","IMPRINT",EDGE,{"derivedFrom":sQuery(id+"F4.wireOp",EDGE,"205f96f4-c8fc-4229-a65b-f430040cf765.1.0.0")}),1.0]])]});
            var Q7;
            Q7=makeQuery(id+"F4.imprint","IMPRINT",FACE,{"disambiguationData":[TD([[makeQuery(id+"F4.imprint","IMPRINT",EDGE,{"derivedFrom":sQuery(id+"F4.wireOp",EDGE,"205f96f4-c8fc-4229-a65b-f430040cf765.2.0.0")}),1.0]])]});
            var Q8;
            Q8=makeQuery(id+"F4.imprint","IMPRINT",FACE,{"disambiguationData":[TD([[makeQuery(id+"F4.imprint","IMPRINT",EDGE,{"derivedFrom":sQuery(id+"F4.wireOp",EDGE,"205f96f4-c8fc-4229-a65b-f430040cf765.3.0.0")}),1.0]])]});
            var Q9;
            Q9=makeQuery(id+"F4.imprint","IMPRINT",FACE,{"disambiguationData":[TD([[makeQuery(id+"F4.imprint","IMPRINT",EDGE,{"derivedFrom":sQuery(id+"F4.wireOp",EDGE,"8d914cb3-9dea-42ac-bea7-a907530d0bcd.1")}),1.0]])]});
            var Q10;
            {var subQ8=sQuery(id+"F4.wireOp",EDGE,"E29");Q10=makeQuery(id+"F4.imprint","IMPRINT",FACE,{"disambiguationData":[TD([[makeQuery(id+"F4.imprint","IMPRINT",EDGE,{"derivedFrom":subQ8}),-1.0]])]});}
            var Q11;
            Q11=makeQuery(id+"F4.imprint","IMPRINT",FACE,{"disambiguationData":[TD([[makeQuery(id+"F4.imprint","IMPRINT",EDGE,{"derivedFrom":sQuery(id+"F4.wireOp",EDGE,"E42.MirrorCS")}),1.0]])]});
            var Q12;
            Q12=makeQuery(id+"F4.imprint","IMPRINT",FACE,{"disambiguationData":[TD([[makeQuery(id+"F4.imprint","IMPRINT",EDGE,{"derivedFrom":sQuery(id+"F4.wireOp",EDGE,"E38.MirrorCS")}),1.0]])]});
            var Q13;
            Q13=makeQuery(id+"F4.imprint","IMPRINT",FACE,{"disambiguationData":[TD([[makeQuery(id+"F4.imprint","IMPRINT",EDGE,{"derivedFrom":sQuery(id+"F4.wireOp",EDGE,"E34.MirrorCS")}),-1.0]])]});
            var Q14;
            Q14=makeQuery(id+"F4.imprint","IMPRINT",FACE,{"disambiguationData":[TD([[makeQuery(id+"F4.imprint","IMPRINT",EDGE,{"derivedFrom":sQuery(id+"F4.wireOp",EDGE,"E32.bottom")}),-1.0]])]});
            var Q15;
            Q15=makeQuery(id+"F4.imprint","IMPRINT",FACE,{"disambiguationData":[TD([[makeQuery(id+"F4.imprint","IMPRINT",EDGE,{"derivedFrom":sQuery(id+"F4.wireOp",EDGE,"E33.1.0.0")}),1.0]])]});
            var Q16;
            Q16=makeQuery(id+"F4.imprint","IMPRINT",FACE,{"disambiguationData":[TD([[makeQuery(id+"F4.imprint","IMPRINT",EDGE,{"derivedFrom":sQuery(id+"F4.wireOp",EDGE,"E33.2.0.0")}),1.0]])]});
            var Q17;
            Q17=makeQuery(id+"F4.imprint","IMPRINT",FACE,{"disambiguationData":[TD([[makeQuery(id+"F4.imprint","IMPRINT",EDGE,{"derivedFrom":sQuery(id+"F4.wireOp",EDGE,"E33.3.0.0")}),1.0]])]});
            var Q18;
            Q18=makeQuery(id+"F4.imprint","IMPRINT",FACE,{"disambiguationData":[TD([[makeQuery(id+"F4.imprint","IMPRINT",EDGE,{"derivedFrom":sQuery(id+"F4.wireOp",EDGE,"E49.MirrorC")}),-1.0]])]});
            var Q19;
            Q19=makeQuery(id+"F4.imprint","IMPRINT",FACE,{"disambiguationData":[TD([[makeQuery(id+"F4.imprint","IMPRINT",EDGE,{"derivedFrom":sQuery(id+"F4.wireOp",EDGE,"E50.MirrorC")}),-1.0]])]});
            var Q20;
            Q20=makeQuery(id+"F4.imprint","IMPRINT",FACE,{"disambiguationData":[TD([[makeQuery(id+"F4.imprint","IMPRINT",EDGE,{"derivedFrom":sQuery(id+"F4.wireOp",EDGE,"E48.MirrorC")}),-1.0]])]});
            var Q21;
            Q21=makeQuery(id+"F4.imprint","IMPRINT",FACE,{"disambiguationData":[TD([[makeQuery(id+"F4.imprint","IMPRINT",EDGE,{"derivedFrom":sQuery(id+"F4.wireOp",EDGE,"E46")}),1.0]])]});
            var Q22;
            Q22=makeQuery(id+"F4.imprint","IMPRINT",FACE,{"disambiguationData":[TD([[makeQuery(id+"F4.imprint","IMPRINT",EDGE,{"derivedFrom":sQuery(id+"F4.wireOp",EDGE,"E47.1.0.0")}),1.0]])]});
            var Q23;
            Q23=makeQuery(id+"F4.imprint","IMPRINT",FACE,{"disambiguationData":[TD([[makeQuery(id+"F4.imprint","IMPRINT",EDGE,{"derivedFrom":sQuery(id+"F4.wireOp",EDGE,"E47.2.0.0")}),1.0]])]});
            var Q24;
            Q24=makeQuery(id+"F4.imprint","IMPRINT",FACE,{"disambiguationData":[TD([[makeQuery(id+"F4.imprint","IMPRINT",EDGE,{"derivedFrom":sQuery(id+"F4.wireOp",EDGE,"E47.3.0.0")}),1.0]])]});
            extrude(context, id + "F6", {"entities" : qUnion([Q0, Q1, Q2, Q3, Q4, Q5, Q6, Q7, Q8, Q9, Q10, Q11, Q12, Q13, Q14, Q15, Q16, Q17, Q18, Q19, Q20, Q21, Q22, Q23, Q24]), "depth" : 4.2 * mm});
        }
        {
            var Q0;
            Q0=qCreatedBy(makeId("Top.planeOp"),FACE);
            var sketch = newSketch(context, id + "F7", { "sketchPlane" : qUnion([Q0])});
            skLineSegment(sketch, "E51.0", {"start": v(-59.16, 10) * mm, "end": v(-17.32, 10) * mm});
            skLineSegment(sketch, "E51.1", {"start": v(-17.32, 10) * mm, "end": v(17.32, 10) * mm});
            skLineSegment(sketch, "E51.2", {"start": v(17.32, 10) * mm, "end": v(59.16, 10) * mm});
            skLineSegment(sketch, "E51.3", {"start": v(17.32, -10) * mm, "end": v(59.16, -10) * mm});
            skLineSegment(sketch, "E51.4", {"start": v(-17.32, -10) * mm, "end": v(17.32, -10) * mm});
            skLineSegment(sketch, "E51.5", {"start": v(-59.16, -10) * mm, "end": v(-17.32, -10) * mm});
            skLineSegment(sketch, "E52.0.0", {"start": v(-43.65, -4.95) * mm, "end": v(-33.75, -4.95) * mm});
            skLineSegment(sketch, "E52.0.1", {"start": v(-33.75, -4.95) * mm, "end": v(-33.75, 4.95) * mm});
            skLineSegment(sketch, "E52.0.2", {"start": v(-33.75, 4.95) * mm, "end": v(-37.7, 4.95) * mm});
            skLineSegment(sketch, "E52.0.3", {"start": v(-43.65, 4.95) * mm, "end": v(-43.65, -4.95) * mm});
            skLineSegment(sketch, "E53.0.0", {"start": v(-30.75, -4.95) * mm, "end": v(-20.85, -4.95) * mm});
            skLineSegment(sketch, "E53.0.1", {"start": v(-20.85, -4.95) * mm, "end": v(-20.85, 4.95) * mm});
            skLineSegment(sketch, "E53.0.2", {"start": v(-20.85, 4.95) * mm, "end": v(-30.75, 4.95) * mm});
            skLineSegment(sketch, "E53.0.3", {"start": v(-30.75, 4.95) * mm, "end": v(-30.75, -4.95) * mm});
            skLineSegment(sketch, "E53.1.0", {"start": v(-7.95, 4.95) * mm, "end": v(-11.9, 4.95) * mm});
            skLineSegment(sketch, "E53.1.1", {"start": v(-17.85, 4.95) * mm, "end": v(-17.85, -4.95) * mm});
            skLineSegment(sketch, "E53.1.2", {"start": v(-17.85, -4.95) * mm, "end": v(-7.95, -4.95) * mm});
            skLineSegment(sketch, "E53.1.3", {"start": v(-7.95, -4.95) * mm, "end": v(-7.95, 4.95) * mm});
            skLineSegment(sketch, "E53.2.0", {"start": v(-4.95, -4.95) * mm, "end": v(4.95, -4.95) * mm});
            skLineSegment(sketch, "E53.2.1", {"start": v(4.95, -4.95) * mm, "end": v(4.95, 4.95) * mm});
            skLineSegment(sketch, "E53.2.2", {"start": v(4.95, 4.95) * mm, "end": v(-4.95, 4.95) * mm});
            skLineSegment(sketch, "E53.2.3", {"start": v(-4.95, 4.95) * mm, "end": v(-4.95, -4.95) * mm});
            skLineSegment(sketch, "E53.3.0", {"start": v(17.85, -4.95) * mm, "end": v(17.85, 4.95) * mm});
            skLineSegment(sketch, "E53.3.1", {"start": v(17.85, 4.95) * mm, "end": v(7.95, 4.95) * mm});
            skLineSegment(sketch, "E53.3.2", {"start": v(7.95, 4.95) * mm, "end": v(7.95, -4.95) * mm});
            skLineSegment(sketch, "E53.3.3", {"start": v(7.95, -4.95) * mm, "end": v(17.85, -4.95) * mm});
            skLineSegment(sketch, "E53.4.0", {"start": v(30.75, -4.95) * mm, "end": v(30.75, 4.95) * mm});
            skLineSegment(sketch, "E53.4.1", {"start": v(30.75, 4.95) * mm, "end": v(20.85, 4.95) * mm});
            skLineSegment(sketch, "E53.4.2", {"start": v(20.85, 4.95) * mm, "end": v(20.85, -4.95) * mm});
            skLineSegment(sketch, "E53.4.3", {"start": v(20.85, -4.95) * mm, "end": v(30.75, -4.95) * mm});
            skLineSegment(sketch, "E53.5.0", {"start": v(43.65, -4.95) * mm, "end": v(43.65, 4.95) * mm});
            skLineSegment(sketch, "E53.5.1", {"start": v(43.65, 4.95) * mm, "end": v(33.75, 4.95) * mm});
            skLineSegment(sketch, "E53.5.2", {"start": v(33.75, 4.95) * mm, "end": v(33.75, -4.95) * mm});
            skLineSegment(sketch, "E53.5.3", {"start": v(33.75, -4.95) * mm, "end": v(43.65, -4.95) * mm});
            skLineSegment(sketch, "E54", {"start": v(-59.53, 7.5) * mm, "end": v(59.53, 7.5) * mm, "construction": true});
            skLineSegment(sketch, "E55", {"start": v(-12.9, 7.5) * mm, "end": v(-12.9, 4.95) * mm, "construction": true});
            skPoint(sketch, "E55.startSnap0", {"position": v(-12.9, 4.95) * mm});
            skLineSegment(sketch, "E56", {"start": v(12.9, 4.95) * mm, "end": v(12.9, 7.5) * mm, "construction": true});
            skLineSegment(sketch, "E57", {"start": v(38.7, 4.95) * mm, "end": v(38.7, 7.5) * mm, "construction": true});
            skLineSegment(sketch, "E58", {"start": v(-59.53, -7.5) * mm, "end": v(59.53, -7.5) * mm, "construction": true});
            skLineSegment(sketch, "E59", {"start": v(-25.8, -4.95) * mm, "end": v(-25.8, -7.5) * mm, "construction": true});
            skLineSegment(sketch, "E60", {"start": v(0, -4.95) * mm, "end": v(0, -7.5) * mm, "construction": true});
            skLineSegment(sketch, "E61", {"start": v(25.8, -4.95) * mm, "end": v(25.8, -7.5) * mm, "construction": true});
            skCircle(sketch, "E62.0", {"center": v(0, 0) * mm, "radius": 60 * mm});
            skLineSegment(sketch, "E63", {"start": v(-38.7, 4.95) * mm, "end": v(-38.7, 7.5) * mm, "construction": true});
            skLineSegment(sketch, "E64.0", {"start": v(-59.4, 8.5) * mm, "end": v(59.4, 8.5) * mm});
            skLineSegment(sketch, "E65.0", {"start": v(-59.65, 6.5) * mm, "end": v(-39.7, 6.5) * mm});
            skLineSegment(sketch, "E66.0", {"start": v(-37.7, 4.95) * mm, "end": v(-37.7, 6.5) * mm});
            skLineSegment(sketch, "E67.0", {"start": v(-39.7, 4.95) * mm, "end": v(-39.7, 6.5) * mm});
            skLineSegment(sketch, "E68.trimOffspring", {"start": v(-37.7, 6.5) * mm, "end": v(59.65, 6.5) * mm});
            skLineSegment(sketch, "E69.0", {"start": v(-13.9, 6.5) * mm, "end": v(-13.9, 4.95) * mm});
            skLineSegment(sketch, "E70.0", {"start": v(-11.9, 6.5) * mm, "end": v(-11.9, 4.95) * mm});
            skLineSegment(sketch, "E71.trimOffspring", {"start": v(-13.9, 4.95) * mm, "end": v(-17.85, 4.95) * mm});
            skLineSegment(sketch, "E72.trimOffspring", {"start": v(-39.7, 4.95) * mm, "end": v(-43.65, 4.95) * mm});
            skLineSegment(sketch, "E73.0", {"start": v(-59.4, -8.5) * mm, "end": v(59.4, -8.5) * mm});
            skLineSegment(sketch, "E74.0", {"start": v(-59.65, -6.5) * mm, "end": v(59.65, -6.5) * mm});
            skLineSegment(sketch, "E75.0", {"start": v(-26.8, -4.95) * mm, "end": v(-26.8, -7.4) * mm});
            skLineSegment(sketch, "E76.0", {"start": v(-24.8, -4.95) * mm, "end": v(-24.8, -7.4) * mm});
            skLineSegment(sketch, "E77.0", {"start": v(-1, -5.05) * mm, "end": v(-1, -7.5) * mm});
            skLineSegment(sketch, "E78.0", {"start": v(1, -5.05) * mm, "end": v(1, -7.5) * mm});
            skLineSegment(sketch, "E79.0", {"start": v(26.8, -4.95) * mm, "end": v(26.8, -7.4) * mm});
            skLineSegment(sketch, "E80.0", {"start": v(24.8, -4.95) * mm, "end": v(24.8, -7.4) * mm});
            skLineSegment(sketch, "E81.0", {"start": v(13.9, 4.95) * mm, "end": v(13.9, 7.4) * mm});
            skLineSegment(sketch, "E82.0", {"start": v(11.9, 4.95) * mm, "end": v(11.9, 7.4) * mm});
            skLineSegment(sketch, "E83.0", {"start": v(39.7, 4.95) * mm, "end": v(39.7, 7.4) * mm});
            skLineSegment(sketch, "E84.0", {"start": v(37.7, 4.95) * mm, "end": v(37.7, 7.4) * mm});
            skCircle(sketch, "E85.0", {"center": v(0, 0) * mm, "radius": 55 * mm});
            skCircle(sketch, "E85.2", {"center": v(0, 0) * mm, "radius": 51.5 * mm});
            skCircle(sketch, "E85.3", {"center": v(0, 0) * mm, "radius": 47.5 * mm});
            skSolve(sketch);
        }
        {
            var Q0;
            Q0=makeQuery(id+"F4.imprint","IMPRINT",FACE,{"disambiguationData":[TD([[makeQuery(id+"F4.imprint","IMPRINT",EDGE,{"derivedFrom":sQuery(id+"F4.wireOp",EDGE,"04902287-73d8-48a6-80b9-1e851868ecae0.MirrorC")}),-1.0]])]});
            var Q1;
            Q1=makeQuery(id+"F4.imprint","IMPRINT",FACE,{"disambiguationData":[TD([[makeQuery(id+"F4.imprint","IMPRINT",EDGE,{"derivedFrom":sQuery(id+"F4.wireOp",EDGE,"8075f1d4-70f9-4dd5-8ec3-b5ab89f9c9bf0.MirrorC")}),-1.0]])]});
            var Q2;
            Q2=makeQuery(id+"F4.imprint","IMPRINT",FACE,{"disambiguationData":[TD([[makeQuery(id+"F4.imprint","IMPRINT",EDGE,{"derivedFrom":sQuery(id+"F4.wireOp",EDGE,"de049f4f-b769-4421-8bf6-e8ee1ef1f7560.MirrorC")}),-1.0]])]});
            var Q3;
            Q3=makeQuery(id+"F4.imprint","IMPRINT",FACE,{"disambiguationData":[TD([[makeQuery(id+"F4.imprint","IMPRINT",EDGE,{"derivedFrom":sQuery(id+"F4.wireOp",EDGE,"8d914cb3-9dea-42ac-bea7-a907530d0bcd.1")}),1.0]])]});
            var Q4;
            Q4=makeQuery(id+"F4.imprint","IMPRINT",FACE,{"disambiguationData":[TD([[makeQuery(id+"F4.imprint","IMPRINT",EDGE,{"derivedFrom":sQuery(id+"F4.wireOp",EDGE,"205f96f4-c8fc-4229-a65b-f430040cf765.1.0.0")}),1.0]])]});
            var Q5;
            Q5=makeQuery(id+"F4.imprint","IMPRINT",FACE,{"disambiguationData":[TD([[makeQuery(id+"F4.imprint","IMPRINT",EDGE,{"derivedFrom":sQuery(id+"F4.wireOp",EDGE,"205f96f4-c8fc-4229-a65b-f430040cf765.2.0.0")}),1.0]])]});
            var Q6;
            Q6=makeQuery(id+"F4.imprint","IMPRINT",FACE,{"disambiguationData":[TD([[makeQuery(id+"F4.imprint","IMPRINT",EDGE,{"derivedFrom":sQuery(id+"F4.wireOp",EDGE,"205f96f4-c8fc-4229-a65b-f430040cf765.3.0.0")}),1.0]])]});
            var Q7;
            {var subQ0=sQuery(id+"F4.wireOp",EDGE,"E27.6");var subQ1=sQuery(id+"F4.wireOp",EDGE,"E27.0");var subQ2=makeQuery(id+"F4.imprint","INTERSECT",VERTEX,{"derivedFrom":[subQ1,subQ0]});Q7=makeQuery(id+"F4.imprint","IMPRINT",FACE,{"disambiguationData":[TD([[makeQuery(id+"F4.imprint","IMPRINT",EDGE,{"disambiguationData":[TD([[subQ2,-1.0]])],"derivedFrom":subQ1}),-1.0]])]});}
            var Q8;
            {var subQ0=sQuery(id+"F4.wireOp",EDGE,"E27.5");var subQ1=sQuery(id+"F4.wireOp",EDGE,"E27.1");var subQ2=makeQuery(id+"F4.imprint","INTERSECT",VERTEX,{"derivedFrom":[subQ1,subQ0]});Q8=makeQuery(id+"F4.imprint","IMPRINT",FACE,{"disambiguationData":[TD([[makeQuery(id+"F4.imprint","IMPRINT",EDGE,{"disambiguationData":[TD([[subQ2,-1.0]])],"derivedFrom":subQ1}),-1.0]])]});}
            var Q9;
            Q9=makeQuery(id+"F4.imprint","IMPRINT",FACE,{"disambiguationData":[TD([[makeQuery(id+"F4.imprint","IMPRINT",EDGE,{"derivedFrom":sQuery(id+"F4.wireOp",EDGE,"E42.MirrorCS")}),1.0]])]});
            var Q10;
            Q10=makeQuery(id+"F4.imprint","IMPRINT",FACE,{"disambiguationData":[TD([[makeQuery(id+"F4.imprint","IMPRINT",EDGE,{"derivedFrom":sQuery(id+"F4.wireOp",EDGE,"E38.MirrorCS")}),1.0]])]});
            var Q11;
            Q11=makeQuery(id+"F4.imprint","IMPRINT",FACE,{"disambiguationData":[TD([[makeQuery(id+"F4.imprint","IMPRINT",EDGE,{"derivedFrom":sQuery(id+"F4.wireOp",EDGE,"E32.bottom")}),-1.0]])]});
            var Q12;
            Q12=makeQuery(id+"F4.imprint","IMPRINT",FACE,{"disambiguationData":[TD([[makeQuery(id+"F4.imprint","IMPRINT",EDGE,{"derivedFrom":sQuery(id+"F4.wireOp",EDGE,"E33.1.0.0")}),1.0]])]});
            var Q13;
            Q13=makeQuery(id+"F4.imprint","IMPRINT",FACE,{"disambiguationData":[TD([[makeQuery(id+"F4.imprint","IMPRINT",EDGE,{"derivedFrom":sQuery(id+"F4.wireOp",EDGE,"E33.2.0.0")}),1.0]])]});
            var Q14;
            Q14=makeQuery(id+"F4.imprint","IMPRINT",FACE,{"disambiguationData":[TD([[makeQuery(id+"F4.imprint","IMPRINT",EDGE,{"derivedFrom":sQuery(id+"F4.wireOp",EDGE,"E33.3.0.0")}),1.0]])]});
            var Q15;
            Q15=makeQuery(id+"F4.imprint","IMPRINT",FACE,{"disambiguationData":[TD([[makeQuery(id+"F4.imprint","IMPRINT",EDGE,{"derivedFrom":sQuery(id+"F4.wireOp",EDGE,"E34.MirrorCS")}),-1.0]])]});
            var Q16;
            Q16=makeQuery(id+"F4.imprint","IMPRINT",FACE,{"disambiguationData":[TD([[makeQuery(id+"F4.imprint","IMPRINT",EDGE,{"derivedFrom":sQuery(id+"F4.wireOp",EDGE,"E50.MirrorC")}),-1.0]])]});
            var Q17;
            Q17=makeQuery(id+"F4.imprint","IMPRINT",FACE,{"disambiguationData":[TD([[makeQuery(id+"F4.imprint","IMPRINT",EDGE,{"derivedFrom":sQuery(id+"F4.wireOp",EDGE,"E49.MirrorC")}),-1.0]])]});
            var Q18;
            Q18=makeQuery(id+"F4.imprint","IMPRINT",FACE,{"disambiguationData":[TD([[makeQuery(id+"F4.imprint","IMPRINT",EDGE,{"derivedFrom":sQuery(id+"F4.wireOp",EDGE,"E48.MirrorC")}),-1.0]])]});
            var Q19;
            Q19=makeQuery(id+"F4.imprint","IMPRINT",FACE,{"disambiguationData":[TD([[makeQuery(id+"F4.imprint","IMPRINT",EDGE,{"derivedFrom":sQuery(id+"F4.wireOp",EDGE,"E46")}),1.0]])]});
            var Q20;
            Q20=makeQuery(id+"F4.imprint","IMPRINT",FACE,{"disambiguationData":[TD([[makeQuery(id+"F4.imprint","IMPRINT",EDGE,{"derivedFrom":sQuery(id+"F4.wireOp",EDGE,"E47.1.0.0")}),1.0]])]});
            var Q21;
            Q21=makeQuery(id+"F4.imprint","IMPRINT",FACE,{"disambiguationData":[TD([[makeQuery(id+"F4.imprint","IMPRINT",EDGE,{"derivedFrom":sQuery(id+"F4.wireOp",EDGE,"E47.2.0.0")}),1.0]])]});
            var Q22;
            Q22=makeQuery(id+"F4.imprint","IMPRINT",FACE,{"disambiguationData":[TD([[makeQuery(id+"F4.imprint","IMPRINT",EDGE,{"derivedFrom":sQuery(id+"F4.wireOp",EDGE,"E47.3.0.0")}),1.0]])]});
            extrude(context, id + "F8", {"entities" : qUnion([Q0, Q1, Q2, Q3, Q4, Q5, Q6, Q7, Q8, Q9, Q10, Q11, Q12, Q13, Q14, Q15, Q16, Q17, Q18, Q19, Q20, Q21, Q22]), "operationType" : NewBodyOperationType.REMOVE, "depth" : 2.1 * mm});
        }
        {
            var Q0;
            Q0=qCreatedBy(makeId("Top.planeOp"),FACE);
            var sketch = newSketch(context, id + "F9", { "sketchPlane" : qUnion([Q0])});
            skLineSegment(sketch, "E86.bottom", {"start": v(9, -9) * mm, "end": v(-9, -9) * mm});
            skLineSegment(sketch, "E86.top", {"start": v(9, 9) * mm, "end": v(-9, 9) * mm});
            skLineSegment(sketch, "E86.left", {"start": v(9, -9) * mm, "end": v(9, 9) * mm});
            skLineSegment(sketch, "E86.right", {"start": v(-9, -9) * mm, "end": v(-9, 9) * mm});
            skPoint(sketch, "E86.middle", {"position": v(0, 0) * mm});
            skLineSegment(sketch, "E87.bottom", {"start": v(4.95, -4.95) * mm, "end": v(-4.95, -4.95) * mm});
            skLineSegment(sketch, "E87.top", {"start": v(4.95, 4.95) * mm, "end": v(-4.95, 4.95) * mm});
            skLineSegment(sketch, "E87.left", {"start": v(4.95, -4.95) * mm, "end": v(4.95, 4.95) * mm});
            skLineSegment(sketch, "E87.right", {"start": v(-4.95, -4.95) * mm, "end": v(-4.95, 4.95) * mm});
            skSolve(sketch);
        }
        {
            var Q0;
            Q0=makeQuery(id+"F9.imprint","IMPRINT",FACE,{"disambiguationData":[TD([[makeQuery(id+"F9.imprint","IMPRINT",EDGE,{"derivedFrom":sQuery(id+"F9.wireOp",EDGE,"E86.bottom")}),-1.0]])]});
            var Q1;
            Q1=makeQuery(id+"F9.imprint","IMPRINT",FACE,{"disambiguationData":[TD([[makeQuery(id+"F9.imprint","IMPRINT",EDGE,{"derivedFrom":sQuery(id+"F9.wireOp",EDGE,"E87.bottom")}),-1.0]])]});
            extrude(context, id + "F10", {"entities" : qUnion([Q0, Q1]), "depth" : 4.2 * mm});
        }
        {
            var Q0;
            Q0=makeQuery(id+"F9.imprint","IMPRINT",FACE,{"disambiguationData":[TD([[makeQuery(id+"F9.imprint","IMPRINT",EDGE,{"derivedFrom":sQuery(id+"F9.wireOp",EDGE,"E87.bottom")}),-1.0]])]});
            extrude(context, id + "F11", {"entities" : qUnion([Q0]), "operationType" : NewBodyOperationType.REMOVE, "depth" : 2.1 * mm});
        }
    });
